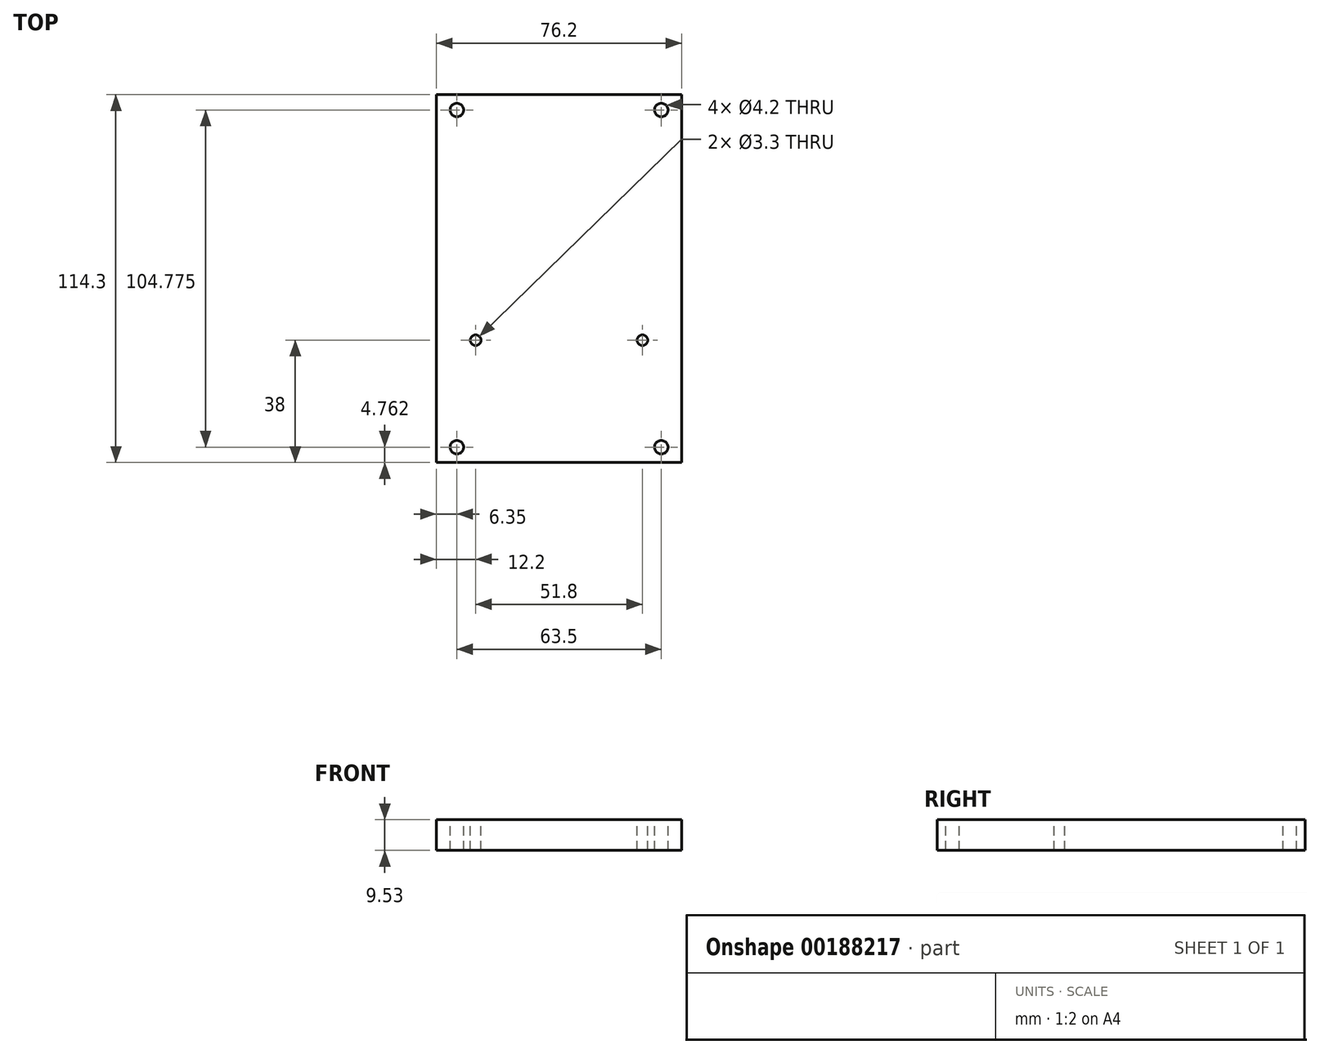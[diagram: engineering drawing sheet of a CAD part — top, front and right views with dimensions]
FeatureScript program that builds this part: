
annotation { "Feature Type Name" : "Feature", "Feature Type Description" : "" }
export const myFeature = defineFeature(function(context is Context, id is Id, definition is map)
    precondition{}
    {
        {
            var Q0;
            Q0=qCreatedBy(makeId("Top.planeOp"),FACE);
            var sketch = newSketch(context, id + "F0", { "sketchPlane" : qUnion([Q0])});
            skLineSegment(sketch, "E0.bottom", {"start": v(38.1, -57.15) * mm, "end": v(-38.1, -57.15) * mm});
            skLineSegment(sketch, "E0.top", {"start": v(38.1, 57.15) * mm, "end": v(-38.1, 57.15) * mm});
            skLineSegment(sketch, "E0.left", {"start": v(38.1, -57.15) * mm, "end": v(38.1, 57.15) * mm});
            skLineSegment(sketch, "E0.right", {"start": v(-38.1, -57.15) * mm, "end": v(-38.1, 57.15) * mm});
            skPoint(sketch, "E0.middle", {"position": v(0, 0) * mm});
            skSolve(sketch);
        }
        {
            var Q0;
            Q0 = qSketchRegion(id + "F0", true);
            extrude(context, id + "F1", {"entities" : qUnion([Q0]), "depth" : 9.52 * mm});
        }
        {
            var Q0;
            Q0=makeQuery(id+"F1.opExtrude","CAP_FACE",FACE,{"disambiguationData":[OSD([sQuery(id+"F0.wireOp",EDGE,"E0.bottom"),sQuery(id+"F0.wireOp",EDGE,"E0.top"),sQuery(id+"F0.wireOp",EDGE,"E0.left"),sQuery(id+"F0.wireOp",EDGE,"E0.right")])],"isStart":false});
            var sketch = newSketch(context, id + "F2", { "sketchPlane" : qUnion([Q0])});
            skPoint(sketch, "E1", {"position": v(-31.75, 52.39) * mm});
            skPoint(sketch, "E2.0.1.0", {"position": v(-31.75, -52.39) * mm});
            skPoint(sketch, "E2.1.0.0", {"position": v(31.75, 52.39) * mm});
            skPoint(sketch, "E2.1.1.0", {"position": v(31.75, -52.39) * mm});
            skLineSegment(sketch, "E2.direction1", {"start": v(-31.75, 52.39) * mm, "end": v(31.75, 52.39) * mm, "construction": true});
            skLineSegment(sketch, "E2.direction2", {"start": v(-31.75, 52.39) * mm, "end": v(-31.75, -52.39) * mm, "construction": true});
            skSolve(sketch);
        }
        {
            var Q0;
            Q0=sQuery(id+"F2.wireOp",VERTEX,"E1");
            var Q1;
            Q1=sQuery(id+"F2.wireOp",VERTEX,"E2.1.0.0");
            var Q2;
            Q2=sQuery(id+"F2.wireOp",VERTEX,"E2.1.1.0");
            var Q3;
            Q3=sQuery(id+"F2.wireOp",VERTEX,"E2.0.1.0");
            var Q4;
            Q4=makeQuery(id+"F1.opExtrude","SWEPT_BODY",BODY,{"disambiguationData":[OSD([sQuery(id+"F0.wireOp",EDGE,"E0.bottom"),sQuery(id+"F0.wireOp",EDGE,"E0.top"),sQuery(id+"F0.wireOp",EDGE,"E0.left"),sQuery(id+"F0.wireOp",EDGE,"E0.right")])]});
            hole(context, id + "F3", {"style" : HoleStyle.SIMPLE, "endStyle" : HoleEndStyle.THROUGH, "standardTappedOrClearance" : lookupTablePath({ "standard" : "ISO", "fit" : "Close", "size" : "M4", "type" : "Clearance" }), "standardBlindInLast" : lookupTablePath({ "fit" : "Close", "standard" : "ISO", "size" : "M4", "type" : "Clearance" }), "holeDiameter" : 4.2 * mm, "startFromSketch" : true, "locations" : qUnion([Q0, Q1, Q2, Q3]), "scope" : qUnion([Q4]), "isTappedThrough" : true});
        }
        {
            var Q0;
            Q0=makeQuery(id+"F1.opExtrude","SWEPT_FACE",FACE,{"disambiguationData":[OSD([sQuery(id+"F0.wireOp",EDGE,"E0.bottom")])]});
            var sketch = newSketch(context, id + "F4", { "sketchPlane" : qUnion([Q0])});
            skCircle(sketch, "E3", {"center": v(0, 6.57) * mm, "radius": 1.27 * mm});
            skSolve(sketch);
        }
        {
            var Q0;
            Q0=makeQuery(id+"F1.opExtrude","CAP_FACE",FACE,{"disambiguationData":[OSD([sQuery(id+"F0.wireOp",EDGE,"E0.bottom"),sQuery(id+"F0.wireOp",EDGE,"E0.top"),sQuery(id+"F0.wireOp",EDGE,"E0.left"),sQuery(id+"F0.wireOp",EDGE,"E0.right")])],"isStart":false});
            var sketch = newSketch(context, id + "F5", { "sketchPlane" : qUnion([Q0])});
            skPoint(sketch, "E4", {"position": v(-25.9, -19.15) * mm});
            skPoint(sketch, "E5", {"position": v(25.9, -19.15) * mm});
            skSolve(sketch);
        }
        {
            var Q0;
            Q0=sQuery(id+"F5.wireOp",VERTEX,"E4");
            var Q1;
            Q1=sQuery(id+"F5.wireOp",VERTEX,"E5");
            var Q2;
            Q2=sQuery(id+"FI7jx1AOZCxDqrO_1.1.F5.wireOp",VERTEX,"E5");
            var Q3;
            Q3=sQuery(id+"FI7jx1AOZCxDqrO_1.1.F5.wireOp",VERTEX,"E4");
            var Q4;
            Q4=makeQuery(id+"F1.opExtrude","SWEPT_BODY",BODY,{"disambiguationData":[OSD([sQuery(id+"F0.wireOp",EDGE,"E0.bottom"),sQuery(id+"F0.wireOp",EDGE,"E0.top"),sQuery(id+"F0.wireOp",EDGE,"E0.left"),sQuery(id+"F0.wireOp",EDGE,"E0.right")])]});
            hole(context, id + "F6", {"style" : HoleStyle.SIMPLE, "endStyle" : HoleEndStyle.BLIND, "standardTappedOrClearance" : lookupTablePath({ "standard" : "ISO", "engagement" : "75%", "pitch" : "0.7 mm", "size" : "M4", "type" : "Tapped" }), "standardBlindInLast" : lookupTablePath({ "standard" : "ISO", "engagement" : "75%", "pitch" : "0.7 mm", "size" : "M4", "type" : "Tapped" }), "holeDiameter" : 3.3 * mm, "holeDepth" : 12 * mm, "startFromSketch" : true, "locations" : qUnion([Q0, Q1, Q2, Q3]), "scope" : qUnion([Q4]), "majorDiameter" : 4 * mm});
        }
    });
